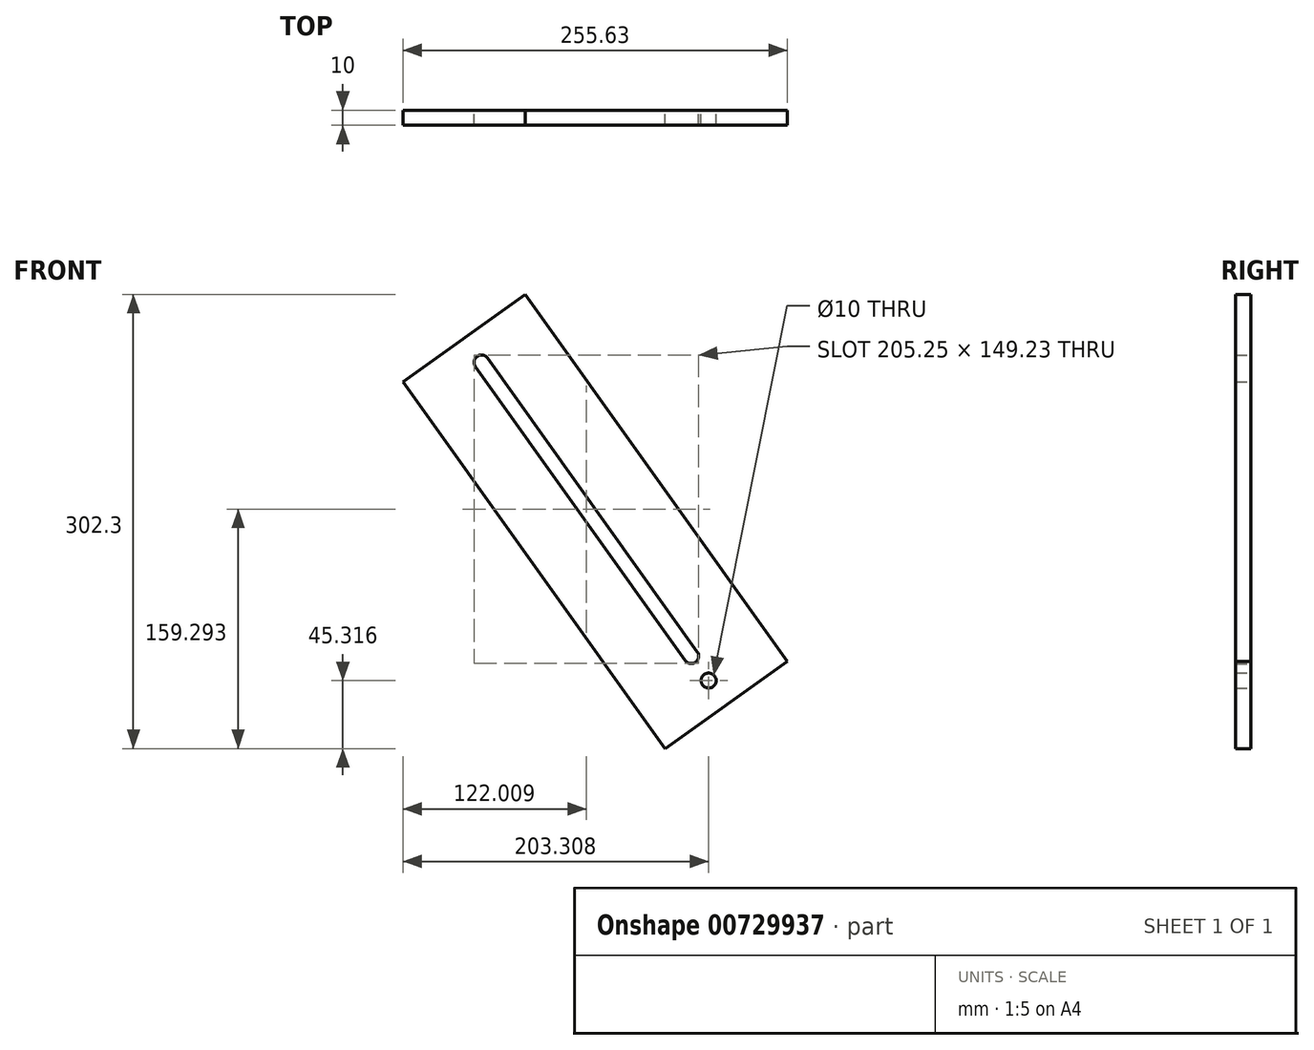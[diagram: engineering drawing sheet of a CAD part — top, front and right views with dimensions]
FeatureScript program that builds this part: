
annotation { "Feature Type Name" : "Feature", "Feature Type Description" : "" }
export const myFeature = defineFeature(function(context is Context, id is Id, definition is map)
    precondition{}
    {
        {
            var Q0;
            Q0=qCreatedBy(makeId("Front.planeOp"),FACE);
            var sketch = newSketch(context, id + "F0", { "sketchPlane" : qUnion([Q0])});
            skLineSegment(sketch, "E0", {"start": v(151.95, 411.06) * mm, "end": v(326.17, 166.83) * mm});
            skLineSegment(sketch, "E1", {"start": v(326.17, 166.83) * mm, "end": v(407.58, 224.9) * mm});
            skLineSegment(sketch, "E2", {"start": v(407.58, 224.9) * mm, "end": v(233.37, 469.13) * mm});
            skLineSegment(sketch, "E3", {"start": v(233.37, 469.13) * mm, "end": v(151.95, 411.06) * mm});
            skLineSegment(sketch, "E4", {"start": v(343.64, 228.43) * mm, "end": v(204.27, 423.82) * mm, "construction": true});
            skLineSegment(sketch, "E5", {"start": v(0, 0) * mm, "end": v(100, 0) * mm, "construction": true});
            skArc(sketch, "E6.0.startCap", {"start": v(347.71, 231.33) * mm, "mid": v(346.55, 224.36) * mm, "end": v(339.57, 225.53) * mm});
            skArc(sketch, "E6.0.endCap", {"start": v(200.2, 420.91) * mm, "mid": v(201.37, 427.89) * mm, "end": v(208.35, 426.72) * mm});
            skLineSegment(sketch, "E6.0.left", {"start": v(339.57, 225.53) * mm, "end": v(200.2, 420.91) * mm});
            skLineSegment(sketch, "E6.0.right", {"start": v(347.71, 231.33) * mm, "end": v(208.35, 426.72) * mm});
            skCircle(sketch, "E7", {"center": v(355.26, 212.15) * mm, "radius": 5 * mm});
            skLineSegment(sketch, "E8", {"start": v(343.64, 228.43) * mm, "end": v(355.26, 212.15) * mm, "construction": true});
            skSolve(sketch);
        }
        {
            var Q0;
            Q0=makeQuery(id+"F0.imprint","IMPRINT",FACE,{"disambiguationData":[TD([[makeQuery(id+"F0.imprint","IMPRINT",EDGE,{"derivedFrom":sQuery(id+"F0.wireOp",EDGE,"E0")}),1.0]])]});
            extrude(context, id + "F1", {"entities" : qUnion([Q0]), "depth" : 10 * mm, "offsetDistance" : 25 * mm});
        }
    });
